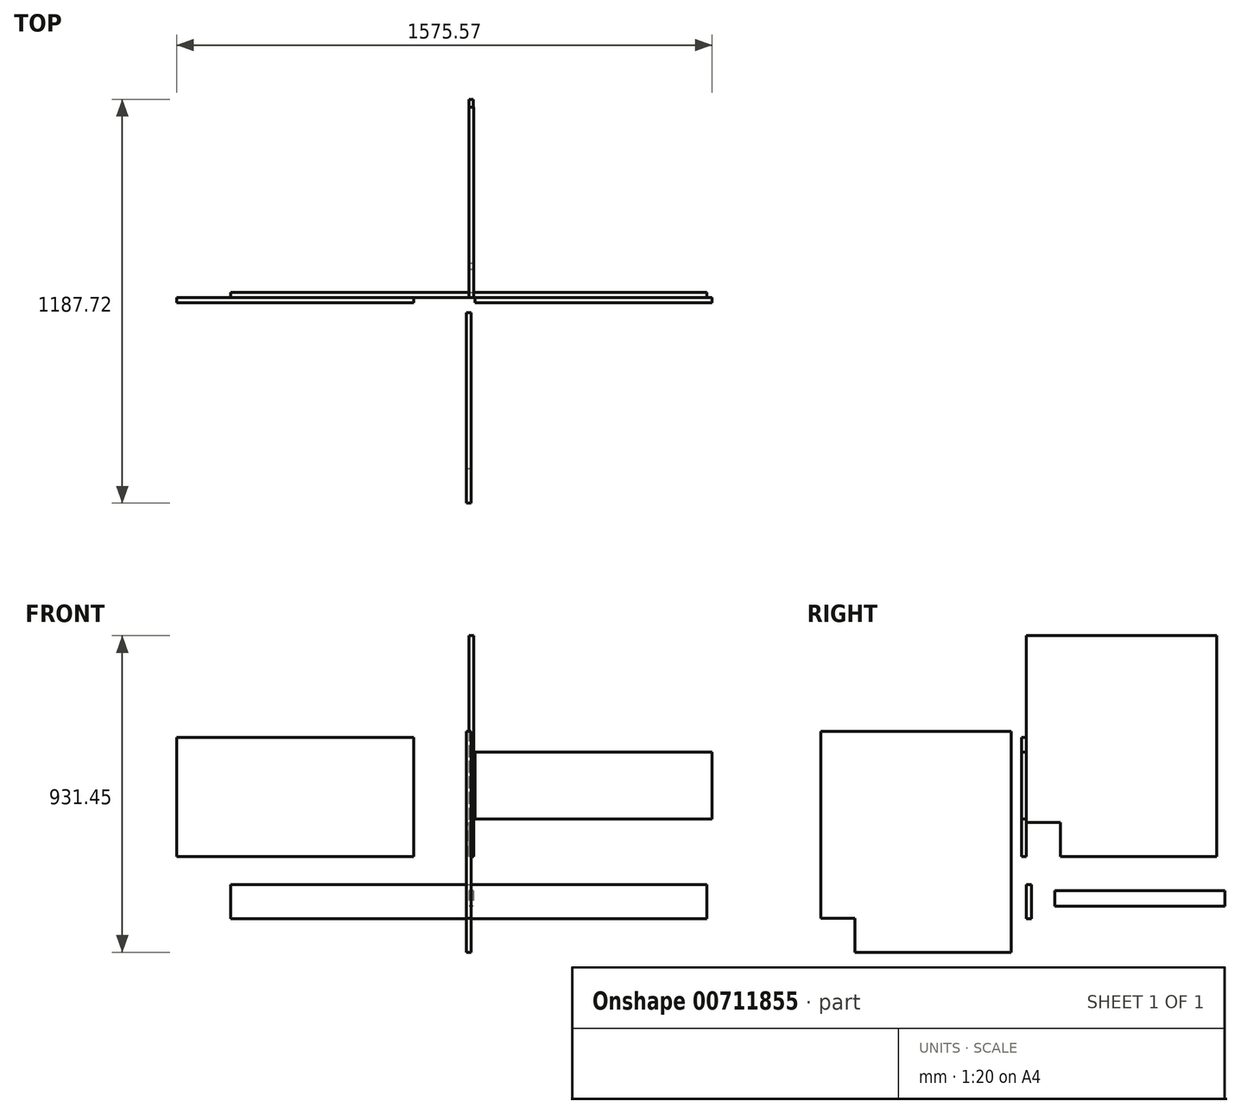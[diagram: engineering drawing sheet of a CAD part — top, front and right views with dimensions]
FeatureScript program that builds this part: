
annotation { "Feature Type Name" : "Feature", "Feature Type Description" : "" }
export const myFeature = defineFeature(function(context is Context, id is Id, definition is map)
    precondition{}
    {
        {
            var Q0;
            Q0=qCreatedBy(makeId("Right.planeOp"),FACE);
            var sketch = newSketch(context, id + "F0", { "sketchPlane" : qUnion([Q0])});
            skLineSegment(sketch, "E0.bottom", {"start": v(0, 650) * mm, "end": v(560, 650) * mm});
            skLineSegment(sketch, "E0.top", {"start": v(100, 0) * mm, "end": v(560, 0) * mm});
            skLineSegment(sketch, "E0.left", {"start": v(0, 650) * mm, "end": v(0, 100) * mm});
            skLineSegment(sketch, "E0.right", {"start": v(560, 650) * mm, "end": v(560, 0) * mm});
            skLineSegment(sketch, "E1.top", {"start": v(0, 100) * mm, "end": v(100, 100) * mm});
            skLineSegment(sketch, "E1.right", {"start": v(100, 0) * mm, "end": v(100, 100) * mm});
            skPoint(sketch, "E2", {"position": v(0, 454) * mm});
            skPoint(sketch, "E3", {"position": v(0, 554) * mm});
            skLineSegment(sketch, "E4", {"start": v(560, 100) * mm, "end": v(0, 100) * mm, "construction": true});
            skSolve(sketch);
        }
        {
            var Q0;
            Q0 = qSketchRegion(id + "F0", true);
            extrude(context, id + "F1", {"entities" : qUnion([Q0]), "depth" : 15 * mm, "offsetDistance" : 25 * mm});
        }
        {
            var Q0;
            Q0=qCreatedBy(makeId("Front.planeOp"),FACE);
            var sketch = newSketch(context, id + "F2", { "sketchPlane" : qUnion([Q0])});
            skLineSegment(sketch, "E5.bottom", {"start": v(-700, -83.07) * mm, "end": v(700, -83.07) * mm});
            skLineSegment(sketch, "E5.top", {"start": v(-700, -183.07) * mm, "end": v(700, -183.07) * mm});
            skLineSegment(sketch, "E5.left", {"start": v(-700, -83.07) * mm, "end": v(-700, -183.07) * mm});
            skLineSegment(sketch, "E5.right", {"start": v(700, -83.07) * mm, "end": v(700, -183.07) * mm});
            skLineSegment(sketch, "E6", {"start": v(0, -83.07) * mm, "end": v(0, -179.45) * mm, "construction": true});
            skSolve(sketch);
        }
        {
            var Q0;
            Q0 = qSketchRegion(id + "F2", true);
            extrude(context, id + "F3", {"entities" : qUnion([Q0]), "oppositeDirection" : true, "depth" : 15 * mm, "offsetDistance" : 25 * mm});
        }
        {
            var Q0;
            Q0=qCreatedBy(makeId("Right.planeOp"),FACE);
            var sketch = newSketch(context, id + "F4", { "sketchPlane" : qUnion([Q0])});
            skLineSegment(sketch, "E7.bottom", {"start": v(-604.48, 368.55) * mm, "end": v(-44.48, 368.55) * mm});
            skLineSegment(sketch, "E7.top", {"start": v(-504.48, -281.45) * mm, "end": v(-44.48, -281.45) * mm});
            skLineSegment(sketch, "E7.left", {"start": v(-604.48, 368.55) * mm, "end": v(-604.48, -181.45) * mm});
            skLineSegment(sketch, "E7.right", {"start": v(-44.48, 368.55) * mm, "end": v(-44.48, -281.45) * mm});
            skLineSegment(sketch, "E8.top", {"start": v(-604.48, -181.45) * mm, "end": v(-504.48, -181.45) * mm});
            skLineSegment(sketch, "E8.right", {"start": v(-504.48, -281.45) * mm, "end": v(-504.48, -181.45) * mm});
            skLineSegment(sketch, "E9", {"start": v(-604.48, -181.45) * mm, "end": v(-44.48, -181.45) * mm, "construction": true});
            skSolve(sketch);
        }
        {
            var Q0;
            Q0 = qSketchRegion(id + "F4", true);
            extrude(context, id + "F5", {"entities" : qUnion([Q0]), "endBound" : BoundingType.SYMMETRIC, "depth" : 15 * mm, "offsetDistance" : 25 * mm});
        }
        {
            var Q0;
            Q0=qCreatedBy(makeId("Front.planeOp"),FACE);
            var sketch = newSketch(context, id + "F6", { "sketchPlane" : qUnion([Q0])});
            skLineSegment(sketch, "E10.bottom", {"start": v(-859.4, 350) * mm, "end": v(-161.4, 350) * mm});
            skLineSegment(sketch, "E10.top", {"start": v(-859.4, 0) * mm, "end": v(-161.4, 0) * mm});
            skLineSegment(sketch, "E10.left", {"start": v(-859.4, 350) * mm, "end": v(-859.4, 0) * mm});
            skLineSegment(sketch, "E10.right", {"start": v(-161.4, 350) * mm, "end": v(-161.4, 0) * mm});
            skSolve(sketch);
        }
        {
            var Q0;
            Q0 = qSketchRegion(id + "F6", true);
            extrude(context, id + "F7", {"entities" : qUnion([Q0]), "depth" : 15 * mm, "offsetDistance" : 25 * mm});
        }
        {
            var Q0;
            Q0=qCreatedBy(makeId("Front.planeOp"),FACE);
            var sketch = newSketch(context, id + "F8", { "sketchPlane" : qUnion([Q0])});
            skLineSegment(sketch, "E11.bottom", {"start": v(18.17, 306.9) * mm, "end": v(716.17, 306.9) * mm});
            skLineSegment(sketch, "E11.top", {"start": v(18.17, 110.9) * mm, "end": v(716.17, 110.9) * mm});
            skLineSegment(sketch, "E11.left", {"start": v(18.17, 306.9) * mm, "end": v(18.17, 110.9) * mm});
            skLineSegment(sketch, "E11.right", {"start": v(716.17, 306.9) * mm, "end": v(716.17, 110.9) * mm});
            skSolve(sketch);
        }
        {
            var Q0;
            Q0 = qSketchRegion(id + "F8", true);
            extrude(context, id + "F9", {"entities" : qUnion([Q0]), "depth" : 15 * mm, "offsetDistance" : 25 * mm});
        }
        {
            var Q0;
            Q0=qCreatedBy(makeId("Right.planeOp"),FACE);
            var sketch = newSketch(context, id + "F10", { "sketchPlane" : qUnion([Q0])});
            skLineSegment(sketch, "E12.bottom", {"start": v(83.24, -99.95) * mm, "end": v(583.24, -99.95) * mm});
            skLineSegment(sketch, "E12.top", {"start": v(83.24, -145.65) * mm, "end": v(583.24, -145.65) * mm});
            skLineSegment(sketch, "E12.left", {"start": v(83.24, -99.95) * mm, "end": v(83.24, -145.65) * mm});
            skLineSegment(sketch, "E12.right", {"start": v(583.24, -99.95) * mm, "end": v(583.24, -145.65) * mm});
            skSolve(sketch);
        }
        {
            var Q0;
            Q0 = qSketchRegion(id + "F10", true);
            extrude(context, id + "F11", {"entities" : qUnion([Q0]), "depth" : 12.7 * mm, "offsetDistance" : 25 * mm});
        }
    });
